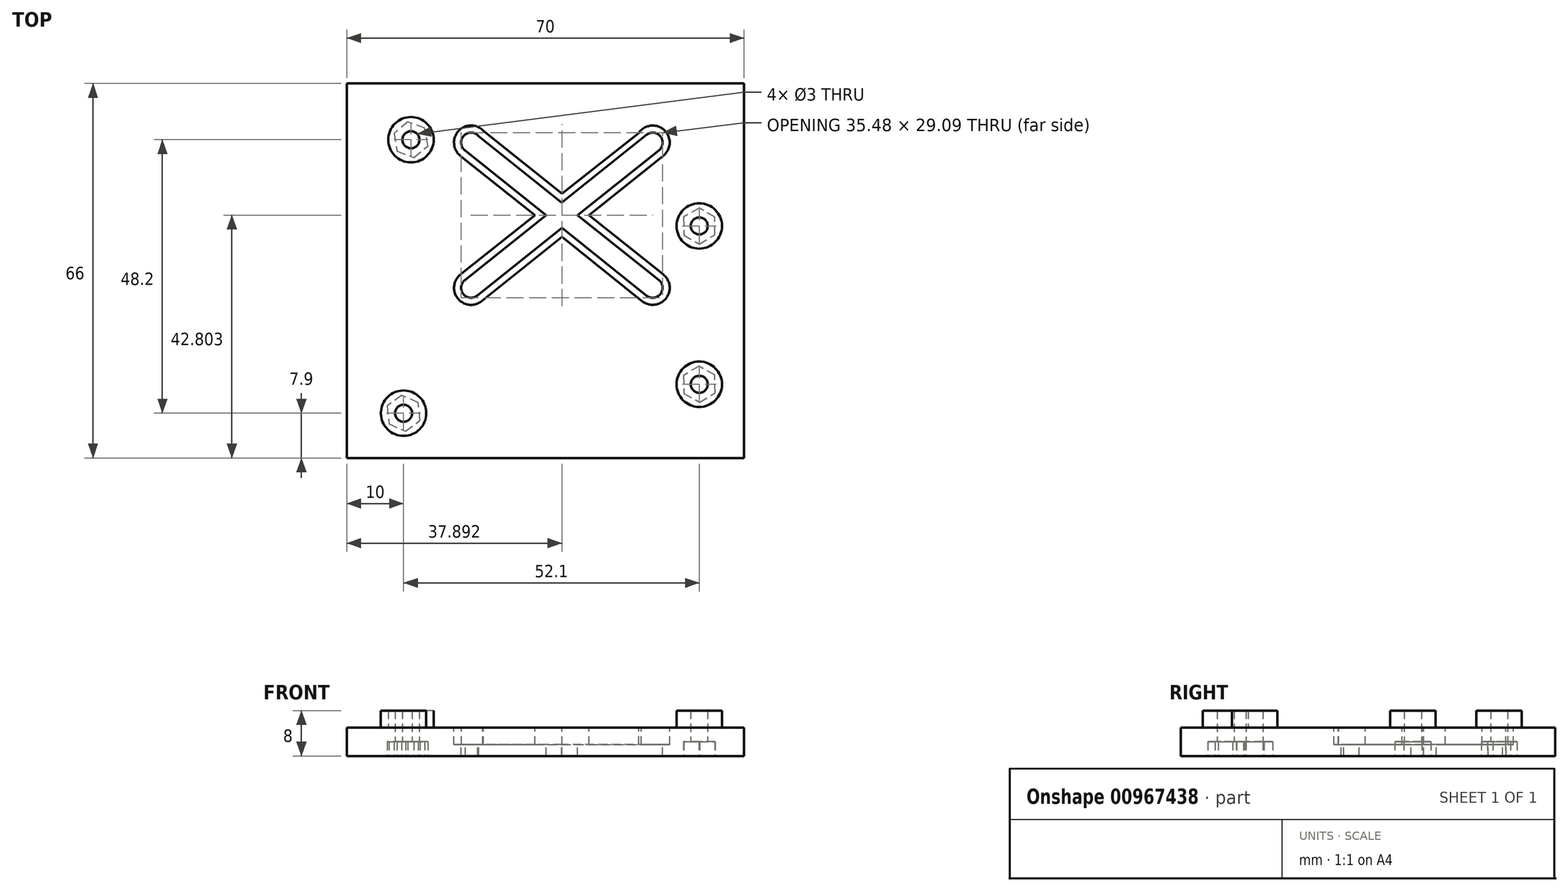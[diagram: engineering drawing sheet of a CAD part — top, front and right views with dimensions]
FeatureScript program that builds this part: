
annotation { "Feature Type Name" : "Feature", "Feature Type Description" : "" }
export const myFeature = defineFeature(function(context is Context, id is Id, definition is map)
    precondition{}
    {
        {
            var Q0;
            Q0=qCreatedBy(makeId("Top.planeOp"),FACE);
            var sketch = newSketch(context, id + "F0", { "sketchPlane" : qUnion([Q0])});
            skLineSegment(sketch, "E0.bottom", {"start": v(-35, 30) * mm, "end": v(35, 30) * mm});
            skLineSegment(sketch, "E0.top", {"start": v(-35, -30) * mm, "end": v(35, -30) * mm});
            skLineSegment(sketch, "E0.left", {"start": v(-35, 30) * mm, "end": v(-35, -30) * mm});
            skLineSegment(sketch, "E0.right", {"start": v(35, 30) * mm, "end": v(35, -30) * mm});
            skPoint(sketch, "E0.middle", {"position": v(0, 0) * mm});
            skSolve(sketch);
        }
        {
            var Q0;
            Q0=qSketchRegion(id+"F0",true);
            extrude(context, id + "F1", {"entities" : qUnion([Q0]), "depth" : 5 * mm, "offsetDistance" : 25 * mm});
        }
        {
            var Q0;
            Q0=makeQuery(id+"F1.opExtrude","CAP_FACE",FACE,{"disambiguationData":[OSD([sQuery(id+"F0.wireOp",EDGE,"E0.bottom"),sQuery(id+"F0.wireOp",EDGE,"E0.top"),sQuery(id+"F0.wireOp",EDGE,"E0.left"),sQuery(id+"F0.wireOp",EDGE,"E0.right")])],"isStart":false});
            var sketch = newSketch(context, id + "F2", { "sketchPlane" : qUnion([Q0])});
            skCircle(sketch, "E1", {"center": v(-23.7, 23.1) * mm, "radius": 4 * mm});
            skCircle(sketch, "E2", {"center": v(-25, -25.1) * mm, "radius": 4 * mm});
            skCircle(sketch, "E3", {"center": v(27.1, 7.9) * mm, "radius": 4 * mm});
            skCircle(sketch, "E4", {"center": v(27.1, -20) * mm, "radius": 4 * mm});
            skSolve(sketch);
        }
        {
            var Q0;
            Q0=qSketchRegion(id+"F2",true);
            extrude(context, id + "F3", {"entities" : qUnion([Q0]), "operationType" : NewBodyOperationType.ADD, "depth" : 3 * mm, "offsetDistance" : 25 * mm});
        }
        {
            var Q0;
            Q0=makeQuery(id+"F1.opExtrude","CAP_FACE",FACE,{"disambiguationData":[OSD([sQuery(id+"F0.wireOp",EDGE,"E0.bottom"),sQuery(id+"F0.wireOp",EDGE,"E0.top"),sQuery(id+"F0.wireOp",EDGE,"E0.left"),sQuery(id+"F0.wireOp",EDGE,"E0.right")])],"isStart":false});
            var sketch = newSketch(context, id + "F4", { "sketchPlane" : qUnion([Q0])});
            skCircle(sketch, "E5", {"center": v(-23.7, 23.1) * mm, "radius": 1.5 * mm});
            skCircle(sketch, "E6", {"center": v(27.1, 7.9) * mm, "radius": 1.5 * mm});
            skCircle(sketch, "E7", {"center": v(27.1, -20) * mm, "radius": 1.5 * mm});
            skCircle(sketch, "E8", {"center": v(-25, -25.1) * mm, "radius": 1.5 * mm});
            skSolve(sketch);
        }
        {
            var Q0;
            Q0=qSketchRegion(id+"F4",true);
            extrude(context, id + "F5", {"entities" : qUnion([Q0]), "operationType" : NewBodyOperationType.REMOVE, "endBound" : BoundingType.THROUGH_ALL, "depth" : 5 * mm, "offsetDistance" : 25 * mm, "hasSecondDirection" : true, "secondDirectionOppositeDirection" : true, "secondDirectionDepth" : 5 * mm});
        }
        {
            var Q0;
            Q0=makeQuery(id+"F1.opExtrude","SWEPT_FACE",FACE,{"disambiguationData":[OSD([sQuery(id+"F0.wireOp",EDGE,"E0.top")])]});
            extrude(context, id + "F6", {"entities" : qUnion([Q0]), "operationType" : NewBodyOperationType.ADD, "depth" : 3 * mm, "offsetDistance" : 25 * mm});
        }
        {
            var Q0;
            Q0=makeQuery(id+"F1.opExtrude","SWEPT_FACE",FACE,{"disambiguationData":[OSD([sQuery(id+"F0.wireOp",EDGE,"E0.bottom")])]});
            extrude(context, id + "F7", {"entities" : qUnion([Q0]), "operationType" : NewBodyOperationType.ADD, "depth" : 3 * mm, "offsetDistance" : 25 * mm});
        }
        {
            var Q0;
            {var subQ0=sQuery(id+"F0.wireOp",EDGE,"E0.left");var subQ1=sQuery(id+"F0.wireOp",EDGE,"E0.bottom");var subQ2=sQuery(id+"F0.wireOp",EDGE,"E0.top");var subQ3=sQuery(id+"F0.wireOp",EDGE,"E0.right");Q0=makeQuery(id+"FJvirERbZmQPNtc_1.boolean.opBoolean","MERGE",FACE,{"derivedFrom":[makeQuery(id+"F4B4IPqYeclfrlC_1.boolean.opBoolean","MERGE",FACE,{"derivedFrom":[makeQuery(id+"F7.boolean.opBoolean","MERGE",FACE,{"derivedFrom":[makeQuery(id+"F6.boolean.opBoolean","MERGE",FACE,{"derivedFrom":[makeQuery(id+"F1.opExtrude","CAP_FACE",FACE,{"disambiguationData":[OSD([subQ1,subQ2,subQ0,subQ3])],"isStart":false}),makeQuery(id+"F6.opExtrude","SWEPT_FACE",FACE,{"disambiguationData":[OSD([subQ2]),TDD([makeQuery(id+"F1.opExtrude","CAP_EDGE",EDGE,{"disambiguationData":[OSD([subQ2])],"isStart":false})])]})]}),makeQuery(id+"F7.opExtrude","SWEPT_FACE",FACE,{"disambiguationData":[OSD([subQ1]),TDD([makeQuery(id+"F1.opExtrude","CAP_EDGE",EDGE,{"disambiguationData":[OSD([subQ1])],"isStart":false})])]})]}),makeQuery(id+"F4B4IPqYeclfrlC_1.opExtrude","SWEPT_FACE",FACE,{"disambiguationData":[OSD([subQ1,subQ2,subQ3]),TDD([makeQuery(id+"F7.boolean.opBoolean","MERGE",EDGE,{"derivedFrom":[makeQuery(id+"F6.boolean.opBoolean","MERGE",EDGE,{"derivedFrom":[makeQuery(id+"F1.opExtrude","CAP_EDGE",EDGE,{"disambiguationData":[OSD([subQ3])],"isStart":false}),makeQuery(id+"F6.opExtrude","SWEPT_EDGE",EDGE,{"disambiguationData":[OSD([subQ2,subQ3]),TDD([makeQuery(id+"F1.opExtrude","CAP_VERTEX",VERTEX,{"disambiguationData":[OSD([subQ2,subQ3])],"isStart":false})])]})]}),makeQuery(id+"F7.opExtrude","SWEPT_EDGE",EDGE,{"disambiguationData":[OSD([subQ1,subQ3]),TDD([makeQuery(id+"F1.opExtrude","CAP_VERTEX",VERTEX,{"disambiguationData":[OSD([subQ1,subQ3])],"isStart":false})])]})]})])]})]}),makeQuery(id+"FJvirERbZmQPNtc_1.opExtrude","SWEPT_FACE",FACE,{"disambiguationData":[OSD([subQ1,subQ2,subQ0]),TDD([makeQuery(id+"F7.boolean.opBoolean","MERGE",EDGE,{"derivedFrom":[makeQuery(id+"F6.boolean.opBoolean","MERGE",EDGE,{"derivedFrom":[makeQuery(id+"F1.opExtrude","CAP_EDGE",EDGE,{"disambiguationData":[OSD([subQ0])],"isStart":false}),makeQuery(id+"F6.opExtrude","SWEPT_EDGE",EDGE,{"disambiguationData":[OSD([subQ2,subQ0]),TDD([makeQuery(id+"F1.opExtrude","CAP_VERTEX",VERTEX,{"disambiguationData":[OSD([subQ2,subQ0])],"isStart":false})])]})]}),makeQuery(id+"F7.opExtrude","SWEPT_EDGE",EDGE,{"disambiguationData":[OSD([subQ1,subQ0]),TDD([makeQuery(id+"F1.opExtrude","CAP_VERTEX",VERTEX,{"disambiguationData":[OSD([subQ1,subQ0])],"isStart":false})])]})]})])]})]});}
            var sketch = newSketch(context, id + "F8", { "sketchPlane" : qUnion([Q0])});
            skArc(sketch, "E9", {"start": v(-14.1, -1.55) * mm, "mid": v(-14.49, -4.08) * mm, "end": v(-11.94, -4.3) * mm});
            skArc(sketch, "E10", {"start": v(-11.76, 23.71) * mm, "mid": v(-14.41, 23.77) * mm, "end": v(-14.07, 21.14) * mm});
            skArc(sketch, "E11", {"start": v(19.98, 21.23) * mm, "mid": v(20.26, 23.7) * mm, "end": v(17.8, 23.97) * mm});
            skArc(sketch, "E12", {"start": v(17.8, -4.37) * mm, "mid": v(20.26, -4.1) * mm, "end": v(19.98, -1.63) * mm});
            skLineSegment(sketch, "E13", {"start": v(-14.3, -1.72) * mm, "end": v(0.1, 9.8) * mm});
            skLineSegment(sketch, "E14", {"start": v(-12.1, -4.43) * mm, "end": v(2.9, 7.56) * mm});
            skLineSegment(sketch, "E15", {"start": v(-11.76, 23.71) * mm, "end": v(2.88, 12.03) * mm});
            skLineSegment(sketch, "E16", {"start": v(-14.32, 21.34) * mm, "end": v(0.1, 9.8) * mm});
            skLineSegment(sketch, "E17.trimOffspring", {"start": v(2.88, 12.03) * mm, "end": v(17.8, 23.97) * mm});
            skLineSegment(sketch, "E18.trimOffspring", {"start": v(5.68, 9.79) * mm, "end": v(19.98, -1.63) * mm});
            skLineSegment(sketch, "E19.trimOffspring", {"start": v(5.68, 9.79) * mm, "end": v(19.98, 21.23) * mm});
            skLineSegment(sketch, "E20.trimOffspring", {"start": v(2.9, 7.56) * mm, "end": v(17.8, -4.37) * mm});
            skSolve(sketch);
        }
        {
            var Q0;
            Q0=qSketchRegion(id+"F8",true);
            extrude(context, id + "F9", {"entities" : qUnion([Q0]), "operationType" : NewBodyOperationType.REMOVE, "oppositeDirection" : true, "depth" : 5 * mm, "offsetDistance" : 25 * mm});
        }
        {
            var Q0;
            {var subQ0=sQuery(id+"F0.wireOp",EDGE,"E0.left");var subQ1=sQuery(id+"F0.wireOp",EDGE,"E0.bottom");var subQ2=sQuery(id+"F0.wireOp",EDGE,"E0.top");var subQ3=sQuery(id+"F0.wireOp",EDGE,"E0.right");Q0=makeQuery(id+"FJvirERbZmQPNtc_1.boolean.opBoolean","MERGE",FACE,{"derivedFrom":[makeQuery(id+"F4B4IPqYeclfrlC_1.boolean.opBoolean","MERGE",FACE,{"derivedFrom":[makeQuery(id+"F7.boolean.opBoolean","MERGE",FACE,{"derivedFrom":[makeQuery(id+"F6.boolean.opBoolean","MERGE",FACE,{"derivedFrom":[makeQuery(id+"F1.opExtrude","CAP_FACE",FACE,{"disambiguationData":[OSD([subQ1,subQ2,subQ0,subQ3])],"isStart":false}),makeQuery(id+"F6.opExtrude","SWEPT_FACE",FACE,{"disambiguationData":[OSD([subQ2]),TDD([makeQuery(id+"F1.opExtrude","CAP_EDGE",EDGE,{"disambiguationData":[OSD([subQ2])],"isStart":false})])]})]}),makeQuery(id+"F7.opExtrude","SWEPT_FACE",FACE,{"disambiguationData":[OSD([subQ1]),TDD([makeQuery(id+"F1.opExtrude","CAP_EDGE",EDGE,{"disambiguationData":[OSD([subQ1])],"isStart":false})])]})]}),makeQuery(id+"F4B4IPqYeclfrlC_1.opExtrude","SWEPT_FACE",FACE,{"disambiguationData":[OSD([subQ1,subQ2,subQ3]),TDD([makeQuery(id+"F7.boolean.opBoolean","MERGE",EDGE,{"derivedFrom":[makeQuery(id+"F6.boolean.opBoolean","MERGE",EDGE,{"derivedFrom":[makeQuery(id+"F1.opExtrude","CAP_EDGE",EDGE,{"disambiguationData":[OSD([subQ3])],"isStart":false}),makeQuery(id+"F6.opExtrude","SWEPT_EDGE",EDGE,{"disambiguationData":[OSD([subQ2,subQ3]),TDD([makeQuery(id+"F1.opExtrude","CAP_VERTEX",VERTEX,{"disambiguationData":[OSD([subQ2,subQ3])],"isStart":false})])]})]}),makeQuery(id+"F7.opExtrude","SWEPT_EDGE",EDGE,{"disambiguationData":[OSD([subQ1,subQ3]),TDD([makeQuery(id+"F1.opExtrude","CAP_VERTEX",VERTEX,{"disambiguationData":[OSD([subQ1,subQ3])],"isStart":false})])]})]})])]})]}),makeQuery(id+"FJvirERbZmQPNtc_1.opExtrude","SWEPT_FACE",FACE,{"disambiguationData":[OSD([subQ1,subQ2,subQ0]),TDD([makeQuery(id+"F7.boolean.opBoolean","MERGE",EDGE,{"derivedFrom":[makeQuery(id+"F6.boolean.opBoolean","MERGE",EDGE,{"derivedFrom":[makeQuery(id+"F1.opExtrude","CAP_EDGE",EDGE,{"disambiguationData":[OSD([subQ0])],"isStart":false}),makeQuery(id+"F6.opExtrude","SWEPT_EDGE",EDGE,{"disambiguationData":[OSD([subQ2,subQ0]),TDD([makeQuery(id+"F1.opExtrude","CAP_VERTEX",VERTEX,{"disambiguationData":[OSD([subQ2,subQ0])],"isStart":false})])]})]}),makeQuery(id+"F7.opExtrude","SWEPT_EDGE",EDGE,{"disambiguationData":[OSD([subQ1,subQ0]),TDD([makeQuery(id+"F1.opExtrude","CAP_VERTEX",VERTEX,{"disambiguationData":[OSD([subQ1,subQ0])],"isStart":false})])]})]})])]})]});}
            var sketch = newSketch(context, id + "F10", { "sketchPlane" : qUnion([Q0])});
            skArc(sketch, "E21", {"start": v(-14.78, -0.5) * mm, "mid": v(-15.46, -4.87) * mm, "end": v(-11.05, -5.18) * mm});
            skArc(sketch, "E22", {"start": v(-10.94, 24.67) * mm, "mid": v(-15.4, 24.53) * mm, "end": v(-14.78, 20.1) * mm});
            skArc(sketch, "E23", {"start": v(20.76, 20.26) * mm, "mid": v(20.93, 24.8) * mm, "end": v(16.41, 24.3) * mm});
            skArc(sketch, "E24", {"start": v(16.9, -5.25) * mm, "mid": v(21.19, -4.93) * mm, "end": v(20.76, -0.66) * mm});
            skLineSegment(sketch, "E25", {"start": v(-14.78, -0.5) * mm, "end": v(-1.86, 9.77) * mm});
            skLineSegment(sketch, "E26", {"start": v(-11.43, -5.49) * mm, "end": v(2.9, 5.97) * mm});
            skLineSegment(sketch, "E27", {"start": v(-10.94, 24.67) * mm, "end": v(2.94, 13.58) * mm});
            skLineSegment(sketch, "E28", {"start": v(-15.18, 20.43) * mm, "end": v(-1.86, 9.77) * mm});
            skLineSegment(sketch, "E29.trimOffspring", {"start": v(2.9, 5.97) * mm, "end": v(17.13, -5.43) * mm});
            skLineSegment(sketch, "E30.trimOffspring", {"start": v(2.94, 13.58) * mm, "end": v(17.8, 25.4) * mm});
            skLineSegment(sketch, "E31.trimOffspring", {"start": v(7.68, 9.8) * mm, "end": v(20.76, -0.66) * mm});
            skLineSegment(sketch, "E32.trimOffspring", {"start": v(7.68, 9.8) * mm, "end": v(20.76, 20.26) * mm});
            skSolve(sketch);
        }
        {
            var Q0;
            Q0=qSketchRegion(id+"F10",true);
            extrude(context, id + "F11", {"entities" : qUnion([Q0]), "operationType" : NewBodyOperationType.REMOVE, "oppositeDirection" : true, "depth" : 3 * mm, "offsetDistance" : 25 * mm});
        }
        {
            var Q0;
            {var subQ0=sQuery(id+"F0.wireOp",EDGE,"E0.left");var subQ1=sQuery(id+"F0.wireOp",EDGE,"E0.bottom");var subQ2=sQuery(id+"F0.wireOp",EDGE,"E0.top");var subQ3=sQuery(id+"F0.wireOp",EDGE,"E0.right");Q0=makeQuery(id+"FJvirERbZmQPNtc_1.boolean.opBoolean","MERGE",FACE,{"derivedFrom":[makeQuery(id+"F4B4IPqYeclfrlC_1.boolean.opBoolean","MERGE",FACE,{"derivedFrom":[makeQuery(id+"F7.boolean.opBoolean","MERGE",FACE,{"derivedFrom":[makeQuery(id+"F6.boolean.opBoolean","MERGE",FACE,{"derivedFrom":[makeQuery(id+"F1.opExtrude","CAP_FACE",FACE,{"disambiguationData":[OSD([subQ1,subQ2,subQ0,subQ3])],"isStart":true}),makeQuery(id+"F6.opExtrude","SWEPT_FACE",FACE,{"disambiguationData":[OSD([subQ2]),TDD([makeQuery(id+"F1.opExtrude","CAP_EDGE",EDGE,{"disambiguationData":[OSD([subQ2])],"isStart":true})])]})]}),makeQuery(id+"F7.opExtrude","SWEPT_FACE",FACE,{"disambiguationData":[OSD([subQ1]),TDD([makeQuery(id+"F1.opExtrude","CAP_EDGE",EDGE,{"disambiguationData":[OSD([subQ1])],"isStart":true})])]})]}),makeQuery(id+"F4B4IPqYeclfrlC_1.opExtrude","SWEPT_FACE",FACE,{"disambiguationData":[OSD([subQ1,subQ2,subQ3]),TDD([makeQuery(id+"F7.boolean.opBoolean","MERGE",EDGE,{"derivedFrom":[makeQuery(id+"F6.boolean.opBoolean","MERGE",EDGE,{"derivedFrom":[makeQuery(id+"F1.opExtrude","CAP_EDGE",EDGE,{"disambiguationData":[OSD([subQ3])],"isStart":true}),makeQuery(id+"F6.opExtrude","SWEPT_EDGE",EDGE,{"disambiguationData":[OSD([subQ2,subQ3]),TDD([makeQuery(id+"F1.opExtrude","CAP_VERTEX",VERTEX,{"disambiguationData":[OSD([subQ2,subQ3])],"isStart":true})])]})]}),makeQuery(id+"F7.opExtrude","SWEPT_EDGE",EDGE,{"disambiguationData":[OSD([subQ1,subQ3]),TDD([makeQuery(id+"F1.opExtrude","CAP_VERTEX",VERTEX,{"disambiguationData":[OSD([subQ1,subQ3])],"isStart":true})])]})]})])]})]}),makeQuery(id+"FJvirERbZmQPNtc_1.opExtrude","SWEPT_FACE",FACE,{"disambiguationData":[OSD([subQ1,subQ2,subQ0]),TDD([makeQuery(id+"F7.boolean.opBoolean","MERGE",EDGE,{"derivedFrom":[makeQuery(id+"F6.boolean.opBoolean","MERGE",EDGE,{"derivedFrom":[makeQuery(id+"F1.opExtrude","CAP_EDGE",EDGE,{"disambiguationData":[OSD([subQ0])],"isStart":true}),makeQuery(id+"F6.opExtrude","SWEPT_EDGE",EDGE,{"disambiguationData":[OSD([subQ2,subQ0]),TDD([makeQuery(id+"F1.opExtrude","CAP_VERTEX",VERTEX,{"disambiguationData":[OSD([subQ2,subQ0])],"isStart":true})])]})]}),makeQuery(id+"F7.opExtrude","SWEPT_EDGE",EDGE,{"disambiguationData":[OSD([subQ1,subQ0]),TDD([makeQuery(id+"F1.opExtrude","CAP_VERTEX",VERTEX,{"disambiguationData":[OSD([subQ1,subQ0])],"isStart":true})])]})]})])]})]});}
            var sketch = newSketch(context, id + "F12", { "sketchPlane" : qUnion([Q0])});
            skCircle(sketch, "E33.cCircle", {"center": v(-25, 25.1) * mm, "radius": 2.75 * mm, "construction": true});
            skLineSegment(sketch, "E33.0", {"start": v(-27.56, 26.98) * mm, "end": v(-24.65, 28.26) * mm});
            skLineSegment(sketch, "E33.1", {"start": v(-24.65, 28.26) * mm, "end": v(-22.1, 26.37) * mm});
            skLineSegment(sketch, "E33.2", {"start": v(-22.1, 26.37) * mm, "end": v(-22.44, 23.22) * mm});
            skLineSegment(sketch, "E33.3", {"start": v(-22.44, 23.22) * mm, "end": v(-25.35, 21.94) * mm});
            skLineSegment(sketch, "E33.4", {"start": v(-25.35, 21.94) * mm, "end": v(-27.9, 23.83) * mm});
            skLineSegment(sketch, "E33.5", {"start": v(-27.9, 23.83) * mm, "end": v(-27.56, 26.98) * mm});
            skPoint(sketch, "E33.0.midPoint", {"position": v(-26.1, 27.62) * mm});
            skCircle(sketch, "E34.cCircle", {"center": v(27.1, 20) * mm, "radius": 2.75 * mm, "construction": true});
            skLineSegment(sketch, "E34.0", {"start": v(24.4, 21.66) * mm, "end": v(27.18, 23.17) * mm});
            skLineSegment(sketch, "E34.1", {"start": v(27.18, 23.17) * mm, "end": v(29.9, 21.52) * mm});
            skLineSegment(sketch, "E34.2", {"start": v(29.9, 21.52) * mm, "end": v(29.8, 18.34) * mm});
            skLineSegment(sketch, "E34.3", {"start": v(29.8, 18.34) * mm, "end": v(27.02, 16.83) * mm});
            skLineSegment(sketch, "E34.4", {"start": v(27.02, 16.83) * mm, "end": v(24.3, 18.48) * mm});
            skLineSegment(sketch, "E34.5", {"start": v(24.3, 18.48) * mm, "end": v(24.4, 21.66) * mm});
            skPoint(sketch, "E34.0.midPoint", {"position": v(25.79, 22.42) * mm});
            skCircle(sketch, "E35.cCircle", {"center": v(27.1, -7.9) * mm, "radius": 2.75 * mm, "construction": true});
            skLineSegment(sketch, "E35.0", {"start": v(24.36, -6.3) * mm, "end": v(27.12, -4.72) * mm});
            skLineSegment(sketch, "E35.1", {"start": v(27.12, -4.72) * mm, "end": v(29.86, -6.33) * mm});
            skLineSegment(sketch, "E35.2", {"start": v(29.86, -6.33) * mm, "end": v(29.84, -9.5) * mm});
            skLineSegment(sketch, "E35.3", {"start": v(29.84, -9.5) * mm, "end": v(27.08, -11.08) * mm});
            skLineSegment(sketch, "E35.4", {"start": v(27.08, -11.08) * mm, "end": v(24.34, -9.47) * mm});
            skLineSegment(sketch, "E35.5", {"start": v(24.34, -9.47) * mm, "end": v(24.36, -6.3) * mm});
            skPoint(sketch, "E35.0.midPoint", {"position": v(25.74, -5.51) * mm});
            skCircle(sketch, "E36.cCircle", {"center": v(-23.7, -23.1) * mm, "radius": 2.75 * mm, "construction": true});
            skLineSegment(sketch, "E36.0", {"start": v(-26.14, -21.06) * mm, "end": v(-23.16, -19.97) * mm});
            skLineSegment(sketch, "E36.1", {"start": v(-23.16, -19.97) * mm, "end": v(-20.72, -22) * mm});
            skLineSegment(sketch, "E36.2", {"start": v(-20.72, -22) * mm, "end": v(-21.26, -25.14) * mm});
            skLineSegment(sketch, "E36.3", {"start": v(-21.26, -25.14) * mm, "end": v(-24.24, -26.23) * mm});
            skLineSegment(sketch, "E36.4", {"start": v(-24.24, -26.23) * mm, "end": v(-26.68, -24.2) * mm});
            skLineSegment(sketch, "E36.5", {"start": v(-26.68, -24.2) * mm, "end": v(-26.14, -21.06) * mm});
            skPoint(sketch, "E36.0.midPoint", {"position": v(-24.65, -20.52) * mm});
            skSolve(sketch);
        }
        {
            var Q0;
            Q0=qSketchRegion(id+"F12",true);
            extrude(context, id + "F13", {"entities" : qUnion([Q0]), "operationType" : NewBodyOperationType.REMOVE, "oppositeDirection" : true, "depth" : 2.5 * mm, "offsetDistance" : 25 * mm});
        }
    });
